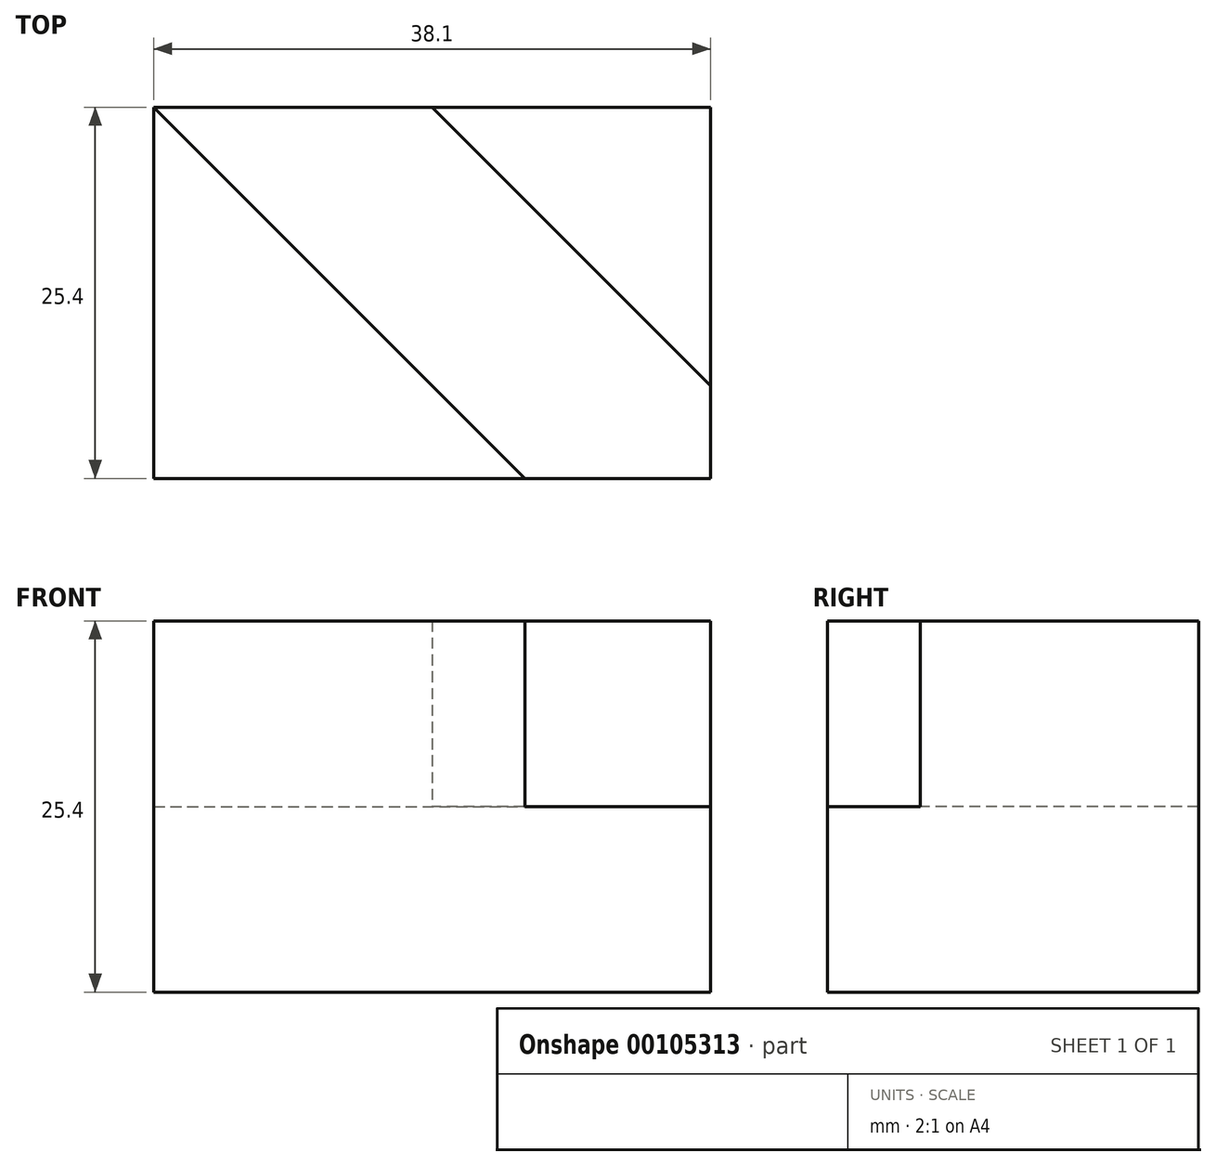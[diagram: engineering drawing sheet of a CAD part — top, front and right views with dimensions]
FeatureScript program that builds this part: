
annotation { "Feature Type Name" : "Feature", "Feature Type Description" : "" }
export const myFeature = defineFeature(function(context is Context, id is Id, definition is map)
    precondition{}
    {
        {
            var Q0;
            Q0=qCreatedBy(makeId("Top.planeOp"),FACE);
            var sketch = newSketch(context, id + "F0", { "sketchPlane" : qUnion([Q0])});
            skLineSegment(sketch, "E0.bottom", {"start": v(0, 0) * mm, "end": v(38.1, 0) * mm});
            skLineSegment(sketch, "E0.top", {"start": v(0, 25.4) * mm, "end": v(38.1, 25.4) * mm});
            skLineSegment(sketch, "E0.left", {"start": v(0, 0) * mm, "end": v(0, 25.4) * mm});
            skLineSegment(sketch, "E0.right", {"start": v(38.1, 0) * mm, "end": v(38.1, 25.4) * mm});
            skLineSegment(sketch, "E1", {"start": v(38.1, 6.35) * mm, "end": v(19.05, 25.4) * mm});
            skLineSegment(sketch, "E2", {"start": v(0, 25.4) * mm, "end": v(25.4, 0) * mm});
            skSolve(sketch);
        }
        {
            var Q0;
            {var subQ0=sQuery(id+"F0.wireOp",EDGE,"E0.left");Q0=makeQuery(id+"F0.imprint","IMPRINT",FACE,{"disambiguationData":[TD([[makeQuery(id+"F0.imprint","IMPRINT",EDGE,{"derivedFrom":subQ0}),-1.0]])]});}
            var Q1;
            {var subQ3=sQuery(id+"F0.wireOp",EDGE,"E1");Q1=makeQuery(id+"F0.imprint","IMPRINT",FACE,{"disambiguationData":[TD([[makeQuery(id+"F0.imprint","IMPRINT",EDGE,{"derivedFrom":subQ3}),-1.0]])]});}
            extrude(context, id + "F1", {"entities" : qUnion([Q0, Q1]), "depth" : 25.4 * mm});
        }
        {
            var Q0;
            {var subQ0=sQuery(id+"F0.wireOp",EDGE,"E1");Q0=makeQuery(id+"F0.imprint","IMPRINT",FACE,{"disambiguationData":[TD([[makeQuery(id+"F0.imprint","IMPRINT",EDGE,{"derivedFrom":subQ0}),1.0]])]});}
            extrude(context, id + "F2", {"entities" : qUnion([Q0]), "operationType" : NewBodyOperationType.ADD, "depth" : 12.7 * mm});
        }
    });
